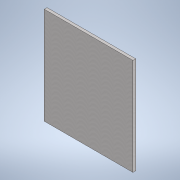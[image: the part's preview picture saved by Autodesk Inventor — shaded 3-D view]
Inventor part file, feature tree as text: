
AUTODESK INVENTOR PART (.ipt)
format: ipt  version: 2021 (Build 250183000, 183)  size: 99,328 bytes
history: native  units: mm
features: extrude x1, sketch x1
ambient origin geometry x8: Origin, YZ Plane, XZ Plane, XY Plane, X Axis, Y Axis, Z Axis, Center Point
bodies: Solid1 (feature_tree)
feature tree (2):
  extrude  "Extrusion1"  Depth=350.0mm
  sketch  "Sketch1"  dims[d0=320.0mm d1=350.0mm d2=10.0mm d3=0.0mm]
